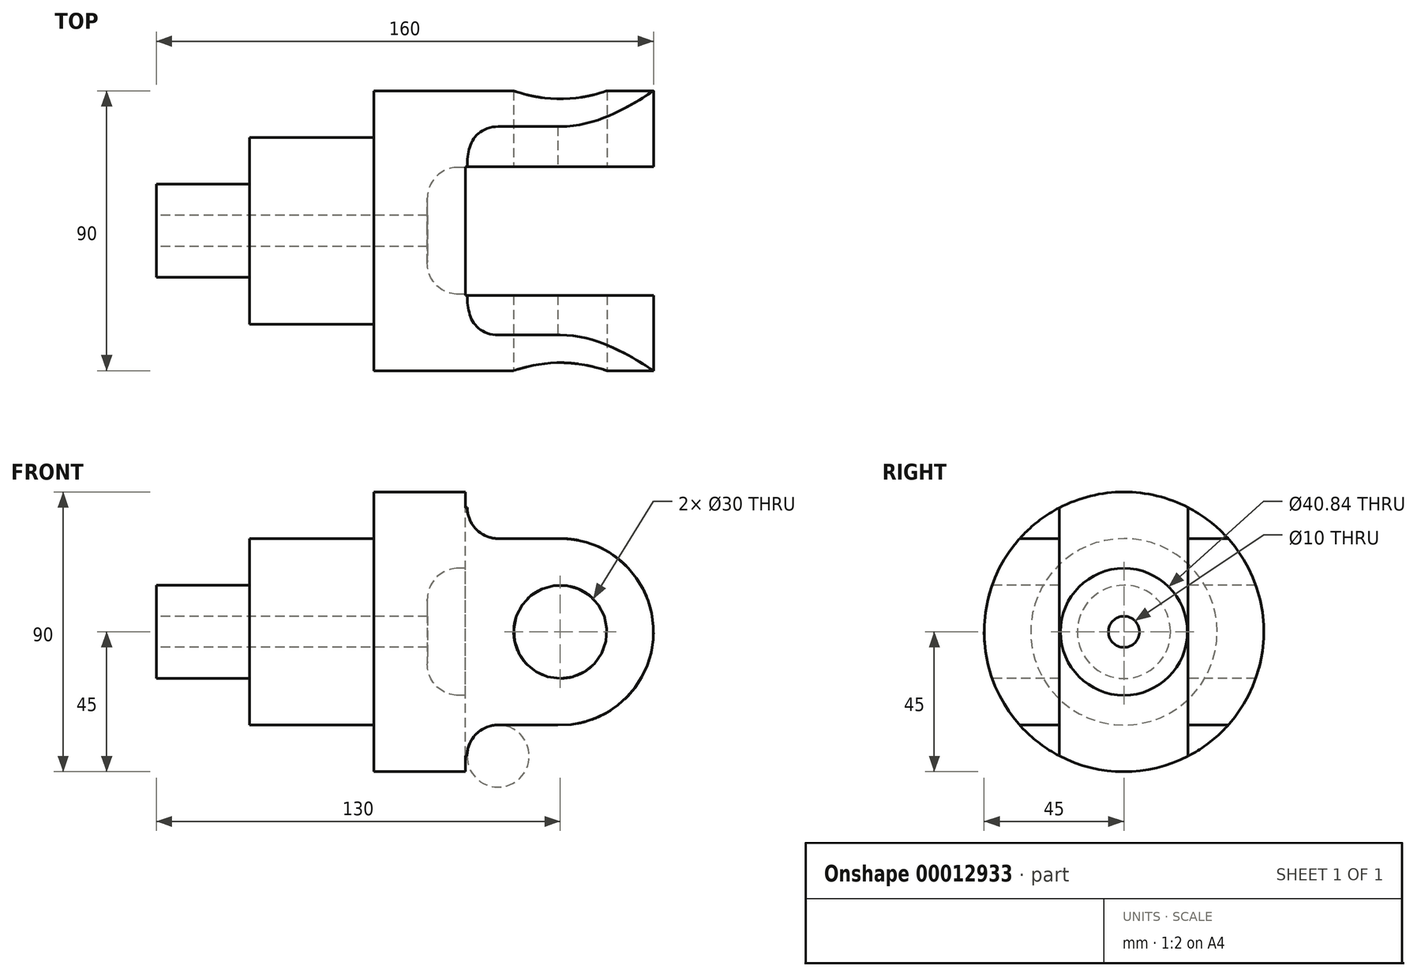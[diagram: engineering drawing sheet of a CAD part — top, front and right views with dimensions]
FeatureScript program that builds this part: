
annotation { "Feature Type Name" : "Feature", "Feature Type Description" : "" }
export const myFeature = defineFeature(function(context is Context, id is Id, definition is map)
    precondition{}
    {
        {
            var Q0;
            Q0=qCreatedBy(makeId("Front.planeOp"),FACE);
            var sketch = newSketch(context, id + "F0", { "sketchPlane" : qUnion([Q0])});
            skLineSegment(sketch, "E0", {"start": v(0, 15) * mm, "end": v(30, 15) * mm});
            skLineSegment(sketch, "E1", {"start": v(30, 15) * mm, "end": v(30, 30) * mm});
            skLineSegment(sketch, "E2", {"start": v(30, 30) * mm, "end": v(70, 30) * mm});
            skLineSegment(sketch, "E3", {"start": v(70, 30) * mm, "end": v(70, 45) * mm});
            skLineSegment(sketch, "E4", {"start": v(70, 45) * mm, "end": v(160, 45) * mm});
            skLineSegment(sketch, "E5", {"start": v(160, 45) * mm, "end": v(160, 20.42) * mm});
            skLineSegment(sketch, "E6", {"start": v(160, 20.42) * mm, "end": v(97.2, 20.42) * mm});
            skArc(sketch, "E7", {"start": v(97.2, 20.42) * mm, "mid": v(90.14, 17.5) * mm, "end": v(87.2, 10.42) * mm});
            skLineSegment(sketch, "E8", {"start": v(0, 15) * mm, "end": v(0, 5) * mm});
            skLineSegment(sketch, "E9", {"start": v(0, 5) * mm, "end": v(87.26, 5) * mm});
            skLineSegment(sketch, "E10", {"start": v(87.26, 5) * mm, "end": v(87.2, 10.42) * mm});
            skLineSegment(sketch, "E11", {"start": v(0, 0) * mm, "end": v(175.95, 0) * mm, "construction": true});
            skSolve(sketch);
        }
        {
            var Q0;
            Q0=makeQuery(id+"F0.imprint","IMPRINT",FACE,{"disambiguationData":[TD([[makeQuery(id+"F0.imprint","IMPRINT",EDGE,{"derivedFrom":sQuery(id+"F0.wireOp",EDGE,"E0")}),-1.0]])]});
            var Q1;
            Q1=sQuery(id+"F0.wireOp",EDGE,"E11");
            revolve(context, id + "F1", {"entities" : qUnion([Q0]), "axis" : qUnion([Q1]), "revolveType" : RevolveType.FULL});
        }
        {
            var Q0;
            Q0=qCreatedBy(makeId("Front.planeOp"),FACE);
            var sketch = newSketch(context, id + "F2", { "sketchPlane" : qUnion([Q0])});
            skLineSegment(sketch, "E12", {"start": v(129.94, 30) * mm, "end": v(110.07, 30) * mm});
            skLineSegment(sketch, "E13", {"start": v(100.07, 40) * mm, "end": v(100.07, 44.77) * mm});
            skCircle(sketch, "E14", {"center": v(130, 0) * mm, "radius": 15 * mm});
            skLineSegment(sketch, "E15", {"start": v(129.18, -29.99) * mm, "end": v(110.02, -29.95) * mm});
            skLineSegment(sketch, "E16", {"start": v(100, -39.95) * mm, "end": v(100, -44.7) * mm});
            skLineSegment(sketch, "E17", {"start": v(100.07, 44.77) * mm, "end": v(162.07, 44.77) * mm});
            skLineSegment(sketch, "E18", {"start": v(162, -45.23) * mm, "end": v(100, -44.7) * mm});
            skArc(sketch, "E19", {"start": v(129.18, -29.99) * mm, "mid": v(160, -0.38) * mm, "end": v(129.94, 30) * mm});
            skLineSegment(sketch, "E20", {"start": v(162.07, 44.77) * mm, "end": v(162, -45.23) * mm});
            skPoint(sketch, "E21.visualSharp", {"position": v(100, -29.93) * mm});
            skArc(sketch, "E21.filletArc", {"start": v(110.02, -29.95) * mm, "mid": v(102.94, -32.87) * mm, "end": v(100, -39.95) * mm});
            skPoint(sketch, "E22.visualSharp", {"position": v(100.07, 30) * mm});
            skArc(sketch, "E22.filletArc", {"start": v(100.07, 40) * mm, "mid": v(103, 32.93) * mm, "end": v(110.07, 30) * mm});
            skSolve(sketch);
        }
        {
            var Q0;
            {var subQ2=sQuery(id+"F2.wireOp",EDGE,"E12");Q0=makeQuery(id+"F2.imprint","IMPRINT",FACE,{"disambiguationData":[TD([[makeQuery(id+"F2.imprint","IMPRINT",EDGE,{"derivedFrom":subQ2}),-1.0]])]});}
            extrude(context, id + "F3", {"entities" : qUnion([Q0]), "operationType" : NewBodyOperationType.REMOVE, "endBound" : BoundingType.SYMMETRIC, "oppositeDirection" : true, "depth" : 90 * mm});
        }
        {
            var Q0;
            Q0=makeQuery(id+"F2.imprint","IMPRINT",FACE,{"disambiguationData":[TD([[makeQuery(id+"F2.imprint","IMPRINT",EDGE,{"derivedFrom":sQuery(id+"F2.wireOp",EDGE,"E14")}),1.0]])]});
            extrude(context, id + "F4", {"entities" : qUnion([Q0]), "operationType" : NewBodyOperationType.REMOVE, "endBound" : BoundingType.SYMMETRIC, "oppositeDirection" : true, "depth" : 90 * mm});
        }
        {
            var Q0;
            Q0=qCreatedBy(makeId("Top.planeOp"),FACE);
            var sketch = newSketch(context, id + "F5", { "sketchPlane" : qUnion([Q0])});
            skLineSegment(sketch, "E23.bottom", {"start": v(160.72, -20.85) * mm, "end": v(99.52, -20.85) * mm});
            skLineSegment(sketch, "E23.top", {"start": v(160.72, 20.65) * mm, "end": v(99.52, 20.65) * mm});
            skLineSegment(sketch, "E23.left", {"start": v(160.72, -20.85) * mm, "end": v(160.72, 20.65) * mm});
            skLineSegment(sketch, "E23.right", {"start": v(99.52, -20.85) * mm, "end": v(99.52, 20.65) * mm});
            skSolve(sketch);
        }
        {
            var Q0;
            Q0=makeQuery(id+"F5.imprint","IMPRINT",FACE,{"disambiguationData":[TD([[makeQuery(id+"F5.imprint","IMPRINT",EDGE,{"derivedFrom":sQuery(id+"F5.wireOp",EDGE,"E23.bottom")}),-1.0]])]});
            extrude(context, id + "F6", {"entities" : qUnion([Q0]), "operationType" : NewBodyOperationType.REMOVE, "endBound" : BoundingType.SYMMETRIC, "oppositeDirection" : true, "depth" : 90 * mm});
        }
    });
